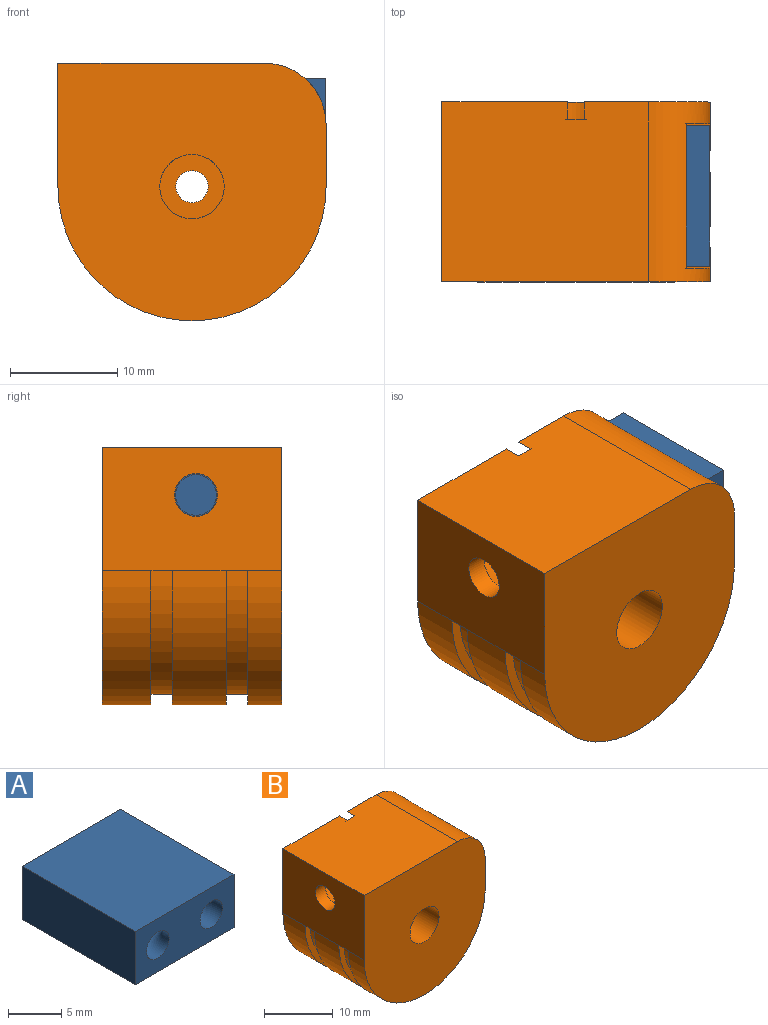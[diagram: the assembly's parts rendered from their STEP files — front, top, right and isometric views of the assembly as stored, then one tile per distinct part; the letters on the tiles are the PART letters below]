
ASSEMBLY  parts=2 mates=1
PART A: 9 faces, bbox 13.1x15x6.1 mm
  f0: plane 15x13.1mm, normal (0,0,-1), area 196.5mm2, adj f1,f3,f4,f7
  f1: plane 15x6.1mm, normal (1,0,0), area 91.5mm2, adj f0,f2,f4,f7
  f2: plane 15x13.1mm, normal (0,0,1), area 196.5mm2, adj f1,f3,f4,f7
  f3: plane 15x6.1mm, normal (-1,0,0), area 91.5mm2, adj f0,f2,f4,f7
  f4: plane 13.1x6.1mm, normal (0,1,0), area 68.6mm2, adj f0,f1,f2,f3,f5
  f5: cylinder r=1.9mm len=9mm, axis (0,1,0), area 107.4mm2, adj f4,f6
  f6: plane 3.8x3.8mm, normal (0,1,0), area 11.3mm2, adj f5
  f7: plane 13.1x6.1mm, normal (0,-1,0), area 65.8mm2, adj f0,f1,f2,f3,f8
  f8: torus R=3.55mm, axis (0,0,-1), area 105.1mm2, adj f7
PART B: 54 faces, bbox 25x16.8x24 mm
  f0: cylinder r=3mm len=13.55mm, axis (0,1,0), area 255.4mm2, adj f11,f50
  f1: plane 19.25x16.75mm, normal (0,0,1), area 319.9mm2, adj f8,f10,f11,f27,f31,f32,f33
  f2: cylinder r=3.6mm len=7.2mm, axis (0,1,0), area 13.6mm2, adj f30,f33
  f3: plane 5x3.8mm, normal (1,0,0), area 19mm2, adj f4,f12,f17,f24
  f4: cylinder r=12.5mm len=25mm, axis (0,1,0), area 196.3mm2, adj f3,f10,f17,f24
  f5: plane 5.75x4.55mm, normal (1,0,0), area 21.2mm2, adj f6,f8,f12,f13,f18,f27
  f6: cylinder r=12.5mm len=25mm, axis (0,1,0), area 178.7mm2, adj f5,f10,f18,f27
  f7: plane 5.75x3.2mm, normal (1,0,0), area 14.6mm2, adj f8,f9,f11,f12,f14,f23
  f8: cylinder r=5.75mm len=16.75mm, axis (0,1,0), area 80.4mm2, adj f1,f5,f7,f11,f13,f14,f15,f27
  f9: cylinder r=12.5mm len=25mm, axis (0,1,0), area 125.7mm2, adj f7,f10,f11,f23
  f10: plane 16.75x11.5mm, normal (-1,0,0), area 180.1mm2, adj f1,f4,f6,f9,f11,f21,f26,f27
  f11: plane 25x24mm, normal (0,-1,0), area 497.6mm2, adj f0,f1,f7,f8,f9,f10
  f12: plane 23x13.5mm, normal (0,0,1), area 302.5mm2, adj f3,f5,f7,f13,f14,f16,f17,f18
  f13: plane 23x6.5mm, normal (0,-1,0), area 146.4mm2, adj f5,f8,f12,f15,f16
  f14: plane 23x6.5mm, normal (0,1,0), area 146.4mm2, adj f7,f8,f12,f15,f16
  f15: plane 20.77x13.5mm, normal (0,0,-1), area 280.3mm2, adj f8,f13,f14,f16
  f16: plane 13.5x6.5mm, normal (1,0,0), area 75.2mm2, adj f12,f13,f14,f15,f53
  f17: plane 25x16.3mm, normal (0,1,0), area 41.7mm2, adj f3,f4,f12,f19,f20,f21,f29
  f18: plane 25x16.3mm, normal (0,-1,0), area 41.7mm2, adj f5,f6,f12,f19,f20,f21,f29
  f19: plane 2.8x2mm, normal (1,0,0), area 5.6mm2, adj f17,f18,f20,f29
  f20: cylinder r=11.5mm len=23mm, axis (0,1,0), area 72.3mm2, adj f17,f18,f19,f21
  f21: plane 2x1mm, normal (0,0,-1), area 2mm2, adj f10,f17,f18,f20
  f22: plane 2.8x2mm, normal (1,0,0), area 5.6mm2, adj f23,f24,f25,f28
  f23: plane 25x16.3mm, normal (0,1,0), area 41.7mm2, adj f7,f9,f12,f22,f25,f26,f28
  f24: plane 25x16.3mm, normal (0,-1,0), area 41.7mm2, adj f3,f4,f12,f22,f25,f26,f28
  f25: cylinder r=11.5mm len=23mm, axis (0,1,0), area 72.3mm2, adj f22,f23,f24,f26
  f26: plane 2x1mm, normal (0,0,-1), area 2mm2, adj f10,f23,f24,f25
  f27: plane 25x24mm, normal (0,1,0), area 293.2mm2, adj f1,f5,f6,f8,f10,f31,f32,f34
  f28: cylinder r=1mm len=2mm, axis (0,1,0), area 3.1mm2, adj f12,f22,f23,f24
  f29: cylinder r=1mm len=2mm, axis (0,1,0), area 3.1mm2, adj f12,f17,f18,f19
  f30: plane 7.2x7.2mm, normal (0,1,0), area 14.3mm2, adj f2,f51
  f31: cylinder r=3.1mm len=3mm, axis (0,1,0), area 6.5mm2, adj f1,f27,f33,f48
  f32: cylinder r=3.1mm len=3mm, axis (0,1,0), area 6.5mm2, adj f1,f27,f33,f34
  f33: plane 23.2x23.1mm, normal (0,1,0), area 192mm2, adj f1,f2,f31,f32,f34,f35,f36,f37
  f34: plane 5.24x1.6mm, normal (-1,0,0), area 8.4mm2, adj f27,f32,f33,f35
  f35: cylinder r=4.5mm len=1.6mm, axis (0,1,0), area 0.4mm2, adj f27,f33,f34,f36
  f36: plane 5.24x1.6mm, normal (0,0,-1), area 8.4mm2, adj f27,f33,f35,f37
  f37: cylinder r=3.1mm len=6.2mm, axis (0,1,0), area 15.6mm2, adj f27,f33,f36,f38
  f38: plane 5.24x1.6mm, normal (0,0,1), area 8.4mm2, adj f27,f33,f37,f39
  f39: cylinder r=4.5mm len=1.6mm, axis (0,1,0), area 0.4mm2, adj f27,f33,f38,f40
  f40: plane 5.24x1.6mm, normal (-1,0,0), area 8.4mm2, adj f27,f33,f39,f41
  f41: cylinder r=3.1mm len=6.2mm, axis (0,1,0), area 15.6mm2, adj f27,f33,f40,f42
  f42: plane 5.24x1.6mm, normal (1,0,0), area 8.4mm2, adj f27,f33,f41,f43
  f43: cylinder r=4.5mm len=1.6mm, axis (0,1,0), area 0.4mm2, adj f27,f33,f42,f44
  f44: plane 5.24x1.6mm, normal (0,0,1), area 8.4mm2, adj f27,f33,f43,f45
  f45: cylinder r=3.1mm len=6.2mm, axis (0,1,0), area 15.6mm2, adj f27,f33,f44,f46
  f46: plane 5.24x1.6mm, normal (0,0,-1), area 8.4mm2, adj f27,f33,f45,f47
  f47: cylinder r=4.5mm len=1.6mm, axis (0,1,0), area 0.4mm2, adj f27,f33,f46,f48
  f48: plane 5.24x1.6mm, normal (1,0,0), area 8.4mm2, adj f27,f31,f33,f47
  f49: cylinder r=1.5mm len=3mm, axis (0,1,0), area 14.1mm2, adj f50,f52
  f50: plane 6x6mm, normal (0,-1,0), area 21.2mm2, adj f0,f49
  f51: cylinder r=2.9mm len=5.8mm, axis (0,-1,0), area 9.1mm2, adj f30,f52
  f52: plane 5.8x5.8mm, normal (0,1,0), area 19.4mm2, adj f49,f51
  f53: cylinder r=2mm len=4mm, axis (-1,0,0), area 25.1mm2, adj f10,f16
PLACE A rot(axis=(0,0,1),90deg) t=(-2.53,-8.75,7.05)mm
PLACE B at identity
MATE slider A.f5 <-> B.f53  axis (-1,0,0) through (-2.53,-8.75,7.05)mm
